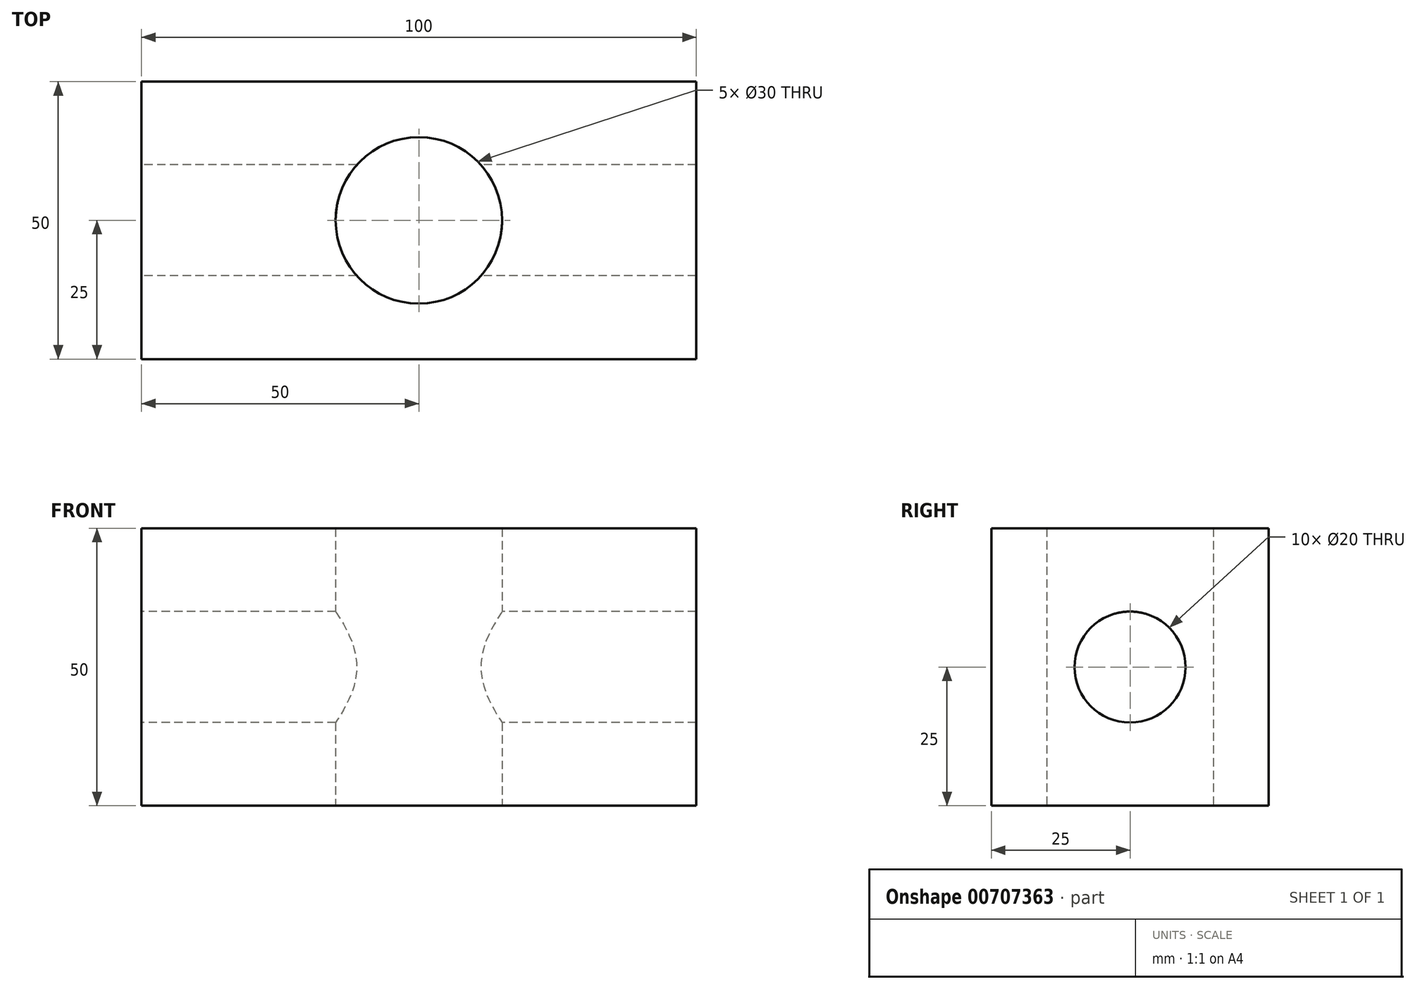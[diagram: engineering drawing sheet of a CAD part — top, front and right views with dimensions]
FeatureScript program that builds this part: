
annotation { "Feature Type Name" : "Feature", "Feature Type Description" : "" }
export const myFeature = defineFeature(function(context is Context, id is Id, definition is map)
    precondition{}
    {
        {
            var Q0;
            Q0=qCreatedBy(makeId("Top.planeOp"),FACE);
            var sketch = newSketch(context, id + "F0", { "sketchPlane" : qUnion([Q0])});
            skLineSegment(sketch, "E0.bottom", {"start": v(-50, 25) * mm, "end": v(50, 25) * mm});
            skLineSegment(sketch, "E0.top", {"start": v(-50, -25) * mm, "end": v(50, -25) * mm});
            skLineSegment(sketch, "E0.left", {"start": v(-50, 25) * mm, "end": v(-50, -25) * mm});
            skLineSegment(sketch, "E0.right", {"start": v(50, 25) * mm, "end": v(50, -25) * mm});
            skCircle(sketch, "E1", {"center": v(0, 0) * mm, "radius": 15 * mm});
            skSolve(sketch);
        }
        {
            var Q0;
            Q0=makeQuery(id+"F0.imprint","IMPRINT",FACE,{"disambiguationData":[TD([[makeQuery(id+"F0.imprint","IMPRINT",EDGE,{"derivedFrom":sQuery(id+"F0.wireOp",EDGE,"E0.bottom")}),-1.0]])]});
            extrude(context, id + "F1", {"entities" : qUnion([Q0]), "depth" : 50 * mm, "offsetDistance" : 25 * mm});
        }
        {
            var Q0;
            Q0=makeQuery(id+"F1.opExtrude","SWEPT_FACE",FACE,{"disambiguationData":[OSD([sQuery(id+"F0.wireOp",EDGE,"E0.left")])]});
            var sketch = newSketch(context, id + "F2", { "sketchPlane" : qUnion([Q0])});
            skCircle(sketch, "E2", {"center": v(0, 25) * mm, "radius": 10 * mm});
            skSolve(sketch);
        }
        {
            var Q0;
            Q0=makeQuery(id+"F2.imprint","IMPRINT",FACE,{"disambiguationData":[TD([[makeQuery(id+"F2.imprint","IMPRINT",EDGE,{"derivedFrom":sQuery(id+"F2.wireOp",EDGE,"E2")}),1.0]])]});
            extrude(context, id + "F3", {"entities" : qUnion([Q0]), "operationType" : NewBodyOperationType.REMOVE, "oppositeDirection" : true, "depth" : 100 * mm, "offsetDistance" : 25 * mm});
        }
    });
